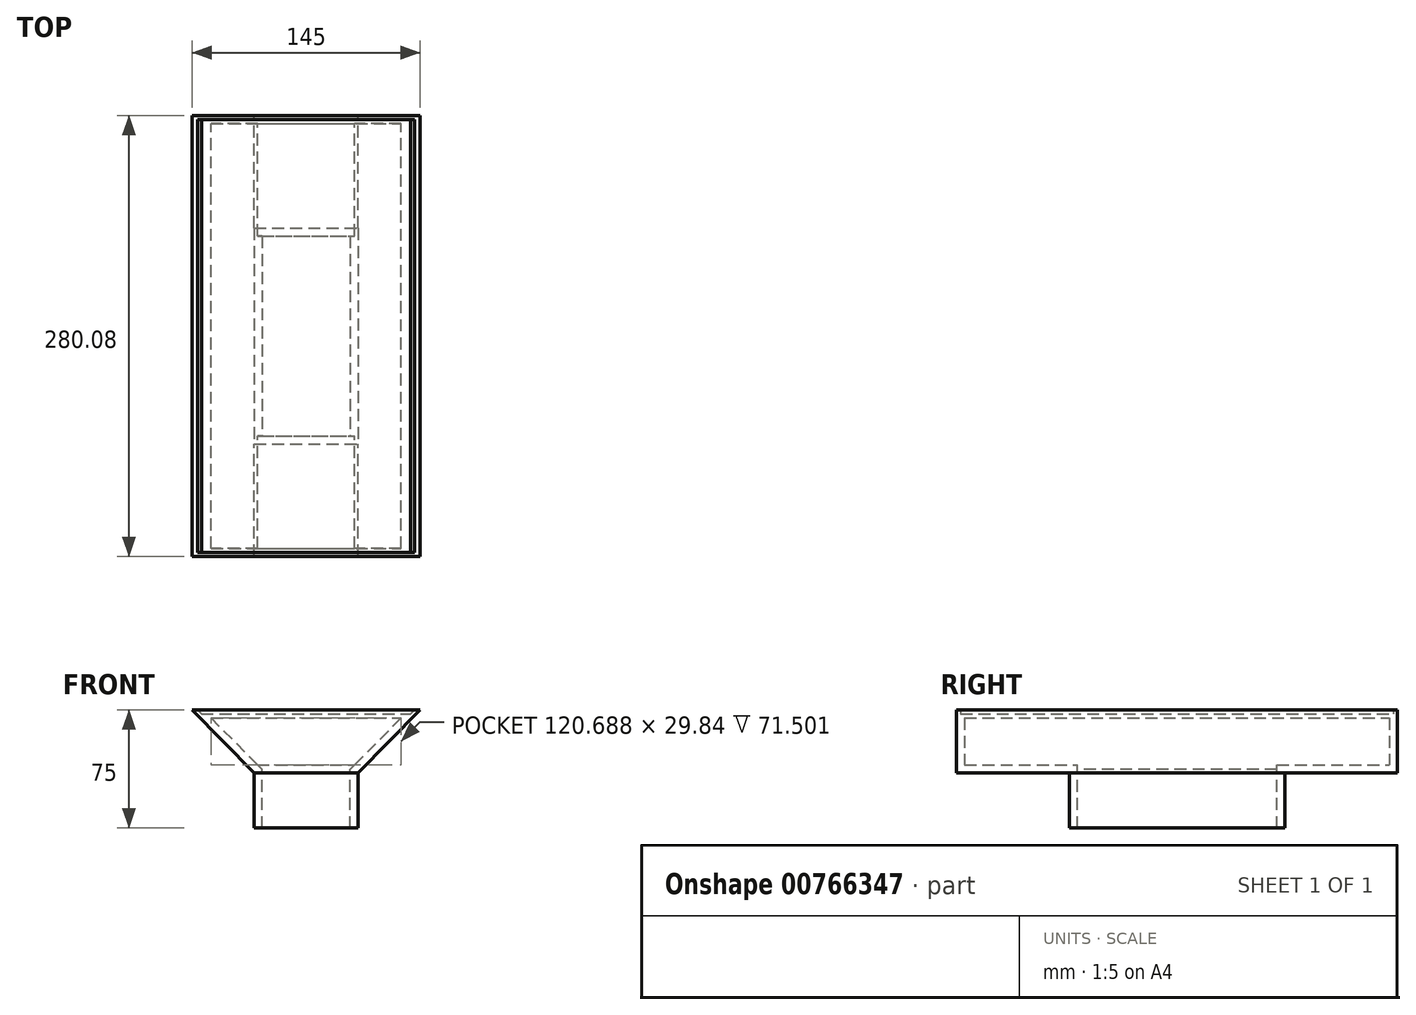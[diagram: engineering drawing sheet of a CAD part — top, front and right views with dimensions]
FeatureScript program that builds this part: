
annotation { "Feature Type Name" : "Feature", "Feature Type Description" : "" }
export const myFeature = defineFeature(function(context is Context, id is Id, definition is map)
    precondition{}
    {
        {
            var Q0;
            Q0=qCreatedBy(makeId("Front.planeOp"),FACE);
            var sketch = newSketch(context, id + "F0", { "sketchPlane" : qUnion([Q0])});
            skLineSegment(sketch, "E0.bottom", {"start": v(-33, -17.5) * mm, "end": v(33, -17.5) * mm});
            skLineSegment(sketch, "E0.top", {"start": v(-33, 17.5) * mm, "end": v(33, 17.5) * mm});
            skLineSegment(sketch, "E0.left", {"start": v(-33, -17.5) * mm, "end": v(-33, 17.5) * mm});
            skLineSegment(sketch, "E0.right", {"start": v(33, -17.5) * mm, "end": v(33, 17.5) * mm});
            skPoint(sketch, "E0.middle", {"position": v(0, 0) * mm});
            skLineSegment(sketch, "E1", {"start": v(0, 0) * mm, "end": v(0, 28.37) * mm});
            skLineSegment(sketch, "E2", {"start": v(-33, 17.5) * mm, "end": v(-72.5, 57.5) * mm});
            skLineSegment(sketch, "E3", {"start": v(-72.5, 57.5) * mm, "end": v(72.5, 57.5) * mm});
            skLineSegment(sketch, "E4", {"start": v(72.5, 57.5) * mm, "end": v(33, 17.5) * mm});
            skSolve(sketch);
        }
        {
            var Q0;
            {var subQ0=sQuery(id+"F0.wireOp",EDGE,"E2");Q0=makeQuery(id+"F0.imprint","IMPRINT",FACE,{"disambiguationData":[TD([[makeQuery(id+"F0.imprint","IMPRINT",EDGE,{"derivedFrom":subQ0}),-1.0]])]});}
            extrude(context, id + "F1", {"entities" : qUnion([Q0]), "depth" : 140.08 * mm, "offsetDistance" : 25.4 * mm});
        }
        {
            var Q0;
            {var subQ0=sQuery(id+"F0.wireOp",EDGE,"E2");Q0=makeQuery(id+"F0.imprint","IMPRINT",FACE,{"disambiguationData":[TD([[makeQuery(id+"F0.imprint","IMPRINT",EDGE,{"derivedFrom":subQ0}),-1.0]])]});}
            extrude(context, id + "F2", {"entities" : qUnion([Q0]), "operationType" : NewBodyOperationType.ADD, "oppositeDirection" : true, "depth" : 140 * mm, "offsetDistance" : 25.4 * mm});
        }
        {
            var Q0;
            Q0=makeQuery(id+"F0.imprint","IMPRINT",FACE,{"disambiguationData":[TD([[makeQuery(id+"F0.imprint","IMPRINT",EDGE,{"derivedFrom":sQuery(id+"F0.wireOp",EDGE,"E0.bottom")}),1.0]])]});
            extrude(context, id + "F3", {"entities" : qUnion([Q0]), "operationType" : NewBodyOperationType.ADD, "oppositeDirection" : true, "depth" : 68.5 * mm, "offsetDistance" : 25.4 * mm});
        }
        {
            var Q0;
            Q0=makeQuery(id+"F0.imprint","IMPRINT",FACE,{"disambiguationData":[TD([[makeQuery(id+"F0.imprint","IMPRINT",EDGE,{"derivedFrom":sQuery(id+"F0.wireOp",EDGE,"E0.bottom")}),1.0]])]});
            extrude(context, id + "F4", {"entities" : qUnion([Q0]), "operationType" : NewBodyOperationType.ADD, "depth" : 68.5 * mm, "offsetDistance" : 25.4 * mm});
        }
        {
            var Q0;
            {var subQ0=sQuery(id+"F0.wireOp",EDGE,"E0.bottom");Q0=makeQuery(id+"F4.boolean.opBoolean","MERGE",FACE,{"derivedFrom":[makeQuery(id+"F3.opExtrude","SWEPT_FACE",FACE,{"disambiguationData":[OSD([subQ0])]}),makeQuery(id+"F4.opExtrude","SWEPT_FACE",FACE,{"disambiguationData":[OSD([subQ0])]})]});}
            shell(context, id + "F5", {"entities" : qUnion([Q0]), "thickness" : 5.08 * mm});
        }
        {
            var Q0;
            {var subQ0=sQuery(id+"F0.wireOp",EDGE,"E3");Q0=makeQuery(id+"F2.boolean.opBoolean","MERGE",FACE,{"derivedFrom":[makeQuery(id+"F1.opExtrude","SWEPT_FACE",FACE,{"disambiguationData":[OSD([subQ0])]}),makeQuery(id+"F2.opExtrude","SWEPT_FACE",FACE,{"disambiguationData":[OSD([subQ0])]})]});}
            shell(context, id + "F6", {"entities" : qUnion([Q0]), "thickness" : 2.54 * mm});
        }
    });
